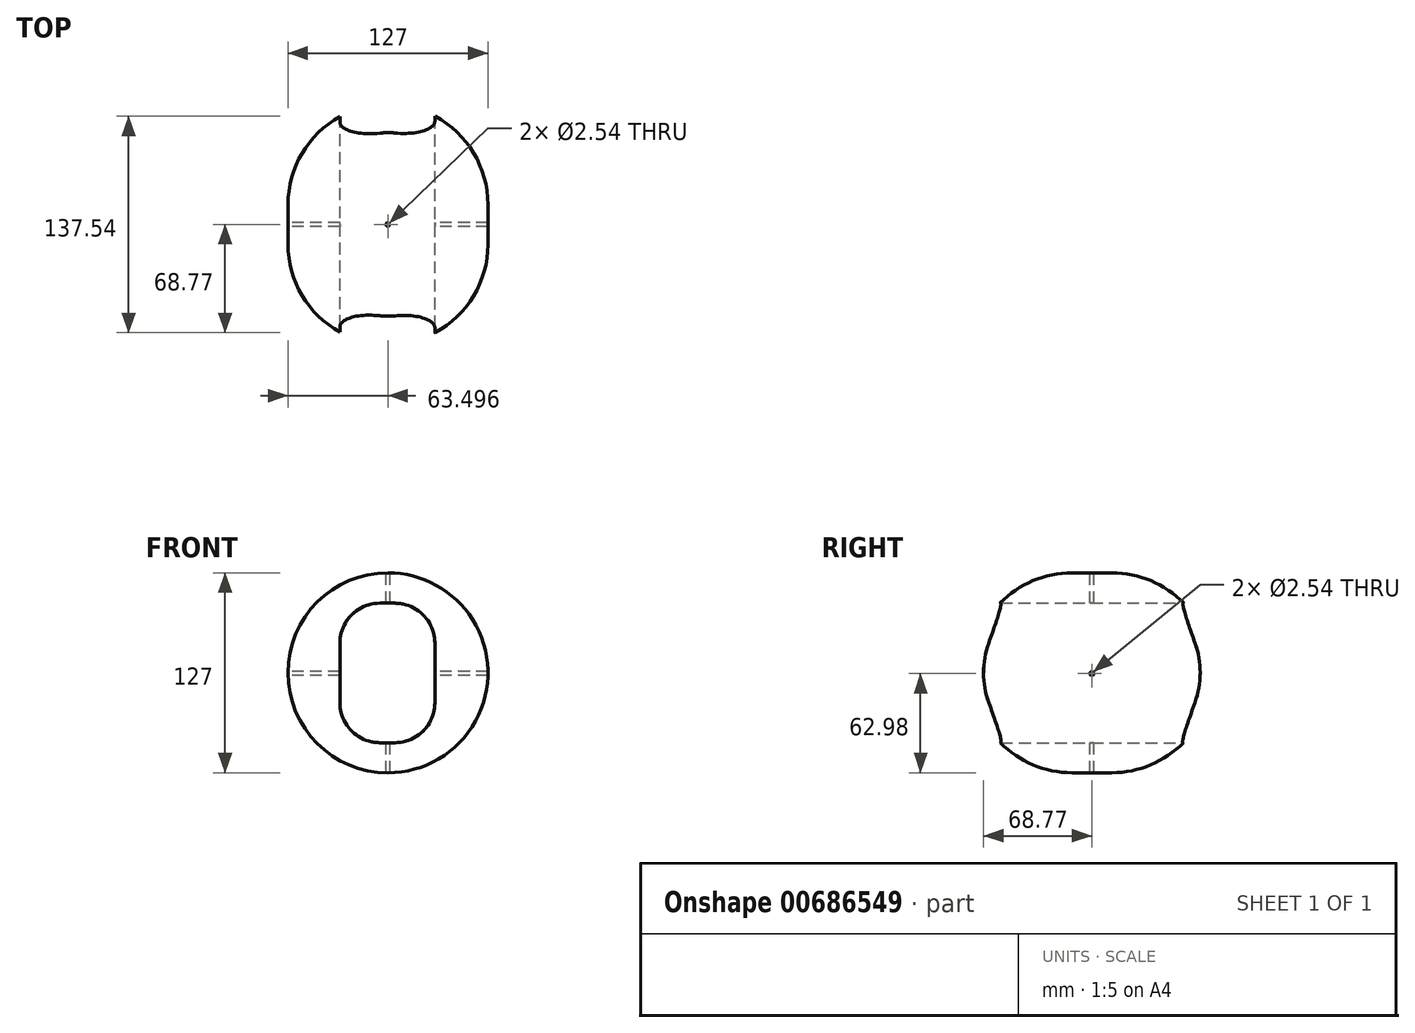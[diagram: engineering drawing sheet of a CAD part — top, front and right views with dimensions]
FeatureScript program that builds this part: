
annotation { "Feature Type Name" : "Feature", "Feature Type Description" : "" }
export const myFeature = defineFeature(function(context is Context, id is Id, definition is map)
    precondition{}
    {
        {
            var Q0;
            Q0=qCreatedBy(makeId("Front.planeOp"),FACE);
            var sketch = newSketch(context, id + "F0", { "sketchPlane" : qUnion([Q0])});
            skLineSegment(sketch, "E0", {"start": v(-48.03, 64.02) * mm, "end": v(-48.03, -62.98) * mm});
            skLineSegment(sketch, "E1", {"start": v(-48.03, -62.98) * mm, "end": v(78.97, -62.98) * mm});
            skLineSegment(sketch, "E2", {"start": v(78.97, -62.98) * mm, "end": v(78.97, 64.02) * mm});
            skLineSegment(sketch, "E3", {"start": v(78.97, 64.02) * mm, "end": v(-48.03, 64.02) * mm});
            skSolve(sketch);
        }
        {
            var Q0;
            Q0 = qSketchRegion(id + "F0", true);
            extrude(context, id + "F1", {"entities" : qUnion([Q0]), "depth" : 152.4 * mm, "offsetDistance" : 25.4 * mm});
        }
        {
            var Q0;
            Q0=makeQuery(id+"F1.opExtrude","SWEPT_EDGE",EDGE,{"disambiguationData":[OSD([sQuery(id+"F0.wireOp",EDGE,"E0"),sQuery(id+"F0.wireOp",EDGE,"E3")])]});
            var Q1;
            Q1=makeQuery(id+"F1.opExtrude","CAP_EDGE",EDGE,{"disambiguationData":[OSD([sQuery(id+"F0.wireOp",EDGE,"E0")])],"isStart":false});
            var Q2;
            Q2=makeQuery(id+"F1.opExtrude","CAP_EDGE",EDGE,{"disambiguationData":[OSD([sQuery(id+"F0.wireOp",EDGE,"E3")])],"isStart":false});
            var Q3;
            Q3=makeQuery(id+"F1.opExtrude","CAP_EDGE",EDGE,{"disambiguationData":[OSD([sQuery(id+"F0.wireOp",EDGE,"E2")])],"isStart":false});
            var Q4;
            Q4=makeQuery(id+"F1.opExtrude","SWEPT_EDGE",EDGE,{"disambiguationData":[OSD([sQuery(id+"F0.wireOp",EDGE,"E2"),sQuery(id+"F0.wireOp",EDGE,"E3")])]});
            var Q5;
            Q5=makeQuery(id+"F1.opExtrude","CAP_EDGE",EDGE,{"disambiguationData":[OSD([sQuery(id+"F0.wireOp",EDGE,"E2")])],"isStart":true});
            var Q6;
            Q6=makeQuery(id+"F1.opExtrude","CAP_EDGE",EDGE,{"disambiguationData":[OSD([sQuery(id+"F0.wireOp",EDGE,"E1")])],"isStart":true});
            var Q7;
            Q7=makeQuery(id+"F1.opExtrude","SWEPT_EDGE",EDGE,{"disambiguationData":[OSD([sQuery(id+"F0.wireOp",EDGE,"E1"),sQuery(id+"F0.wireOp",EDGE,"E2")])]});
            var Q8;
            Q8=makeQuery(id+"F1.opExtrude","SWEPT_EDGE",EDGE,{"disambiguationData":[OSD([sQuery(id+"F0.wireOp",EDGE,"E0"),sQuery(id+"F0.wireOp",EDGE,"E1")])]});
            var Q9;
            Q9=makeQuery(id+"F1.opExtrude","CAP_EDGE",EDGE,{"disambiguationData":[OSD([sQuery(id+"F0.wireOp",EDGE,"E0")])],"isStart":true});
            var Q10;
            Q10=makeQuery(id+"F1.opExtrude","CAP_EDGE",EDGE,{"disambiguationData":[OSD([sQuery(id+"F0.wireOp",EDGE,"E1")])],"isStart":false});
            var Q11;
            Q11=makeQuery(id+"F1.opExtrude","CAP_EDGE",EDGE,{"disambiguationData":[OSD([sQuery(id+"F0.wireOp",EDGE,"E3")])],"isStart":true});
            fillet(context, id + "F2", {"entities" : qUnion([Q0, Q1, Q2, Q3, Q4, Q5, Q6, Q7, Q8, Q9, Q10, Q11]), "radius" : 63.5 * mm, "tangentPropagation" : true, "allowEdgeOverflow" : false});
        }
        {
            var Q0;
            Q0=qCreatedBy(makeId("Front.planeOp"),FACE);
            var sketch = newSketch(context, id + "F3", { "sketchPlane" : qUnion([Q0])});
            skLineSegment(sketch, "E4", {"start": v(-15.09, 44.71) * mm, "end": v(-15.09, -43.88) * mm});
            skLineSegment(sketch, "E5", {"start": v(-15.09, -43.88) * mm, "end": v(45.26, -43.88) * mm});
            skLineSegment(sketch, "E6", {"start": v(45.26, -43.88) * mm, "end": v(45.26, 44.71) * mm});
            skLineSegment(sketch, "E7", {"start": v(45.26, 44.71) * mm, "end": v(-15.09, 44.71) * mm});
            skSolve(sketch);
        }
        {
            var Q0;
            Q0 = qSketchRegion(id + "F3", true);
            extrude(context, id + "F4", {"entities" : qUnion([Q0]), "operationType" : NewBodyOperationType.REMOVE, "depth" : 187.7 * mm, "offsetDistance" : 25.4 * mm});
        }
        {
            var Q0;
            Q0=makeQuery(id+"F4.boolean.opBoolean","COPY",EDGE,{"derivedFrom":makeQuery(id+"F4.opExtrude","SWEPT_EDGE",EDGE,{"disambiguationData":[OSD([sQuery(id+"F3.wireOp",EDGE,"E5"),sQuery(id+"F3.wireOp",EDGE,"E6")])]})});
            var Q1;
            Q1=makeQuery(id+"F4.boolean.opBoolean","COPY",EDGE,{"derivedFrom":makeQuery(id+"F4.opExtrude","SWEPT_EDGE",EDGE,{"disambiguationData":[OSD([sQuery(id+"F3.wireOp",EDGE,"E6"),sQuery(id+"F3.wireOp",EDGE,"E7")])]})});
            var Q2;
            Q2=makeQuery(id+"F4.boolean.opBoolean","COPY",EDGE,{"derivedFrom":makeQuery(id+"F4.opExtrude","SWEPT_EDGE",EDGE,{"disambiguationData":[OSD([sQuery(id+"F3.wireOp",EDGE,"E4"),sQuery(id+"F3.wireOp",EDGE,"E7")])]})});
            var Q3;
            Q3=makeQuery(id+"F4.boolean.opBoolean","COPY",EDGE,{"derivedFrom":makeQuery(id+"F4.opExtrude","SWEPT_EDGE",EDGE,{"disambiguationData":[OSD([sQuery(id+"F3.wireOp",EDGE,"E4"),sQuery(id+"F3.wireOp",EDGE,"E5")])]})});
            fillet(context, id + "F5", {"entities" : qUnion([Q0, Q1, Q2, Q3]), "radius" : 25.4 * mm, "tangentPropagation" : true, "allowEdgeOverflow" : false});
        }
        {
            var Q0;
            Q0=qCreatedBy(makeId("Top.planeOp"),FACE);
            var sketch = newSketch(context, id + "F6", { "sketchPlane" : qUnion([Q0])});
            skLineSegment(sketch, "E8", {"start": v(78.97, -63.5) * mm, "end": v(78.97, -88.9) * mm});
            skLineSegment(sketch, "E9", {"start": v(-48.03, -88.9) * mm, "end": v(-48.03, -63.5) * mm});
            skLineSegment(sketch, "E10", {"start": v(-48.03, -76.2) * mm, "end": v(78.97, -76.2) * mm, "construction": true});
            skLineSegment(sketch, "E11", {"start": v(15.47, -76.2) * mm, "end": v(15.47, -63.44) * mm, "construction": true});
            skLineSegment(sketch, "E12", {"start": v(15.47, -63.44) * mm, "end": v(15.47, -88.47) * mm, "construction": true});
            skCircle(sketch, "E13", {"center": v(15.47, -76.2) * mm, "radius": 1.27 * mm});
            skSolve(sketch);
        }
        {
            var Q0;
            Q0 = qSketchRegion(id + "F6", true);
            extrude(context, id + "F7", {"entities" : qUnion([Q0]), "operationType" : NewBodyOperationType.REMOVE, "endBound" : BoundingType.THROUGH_ALL, "oppositeDirection" : true, "depth" : 66.8 * mm, "offsetDistance" : 25.4 * mm, "hasSecondDirection" : true, "secondDirectionOppositeDirection" : false, "secondDirectionDepth" : 95.76 * mm});
        }
        {
            var Q0;
            Q0=qCreatedBy(makeId("Right.planeOp"),FACE);
            var sketch = newSketch(context, id + "F8", { "sketchPlane" : qUnion([Q0])});
            skLineSegment(sketch, "E14", {"start": v(-63.5, -62.98) * mm, "end": v(-88.9, -62.98) * mm});
            skLineSegment(sketch, "E15", {"start": v(-88.9, 64.02) * mm, "end": v(-63.5, 64.02) * mm});
            skLineSegment(sketch, "E16", {"start": v(-76.2, 64.02) * mm, "end": v(-76.2, -62.98) * mm, "construction": true});
            skCircle(sketch, "E17", {"center": v(-76.2, 0) * mm, "radius": 1.27 * mm});
            skSolve(sketch);
        }
        {
            var Q0;
            Q0 = qSketchRegion(id + "F8", true);
            extrude(context, id + "F9", {"entities" : qUnion([Q0]), "operationType" : NewBodyOperationType.REMOVE, "endBound" : BoundingType.THROUGH_ALL, "depth" : 25.4 * mm, "offsetDistance" : 25.4 * mm, "hasSecondDirection" : true, "secondDirectionBound" : SecondDirectionBoundingType.THROUGH_ALL, "secondDirectionOppositeDirection" : true, "secondDirectionDepth" : 25.4 * mm});
        }
    });
